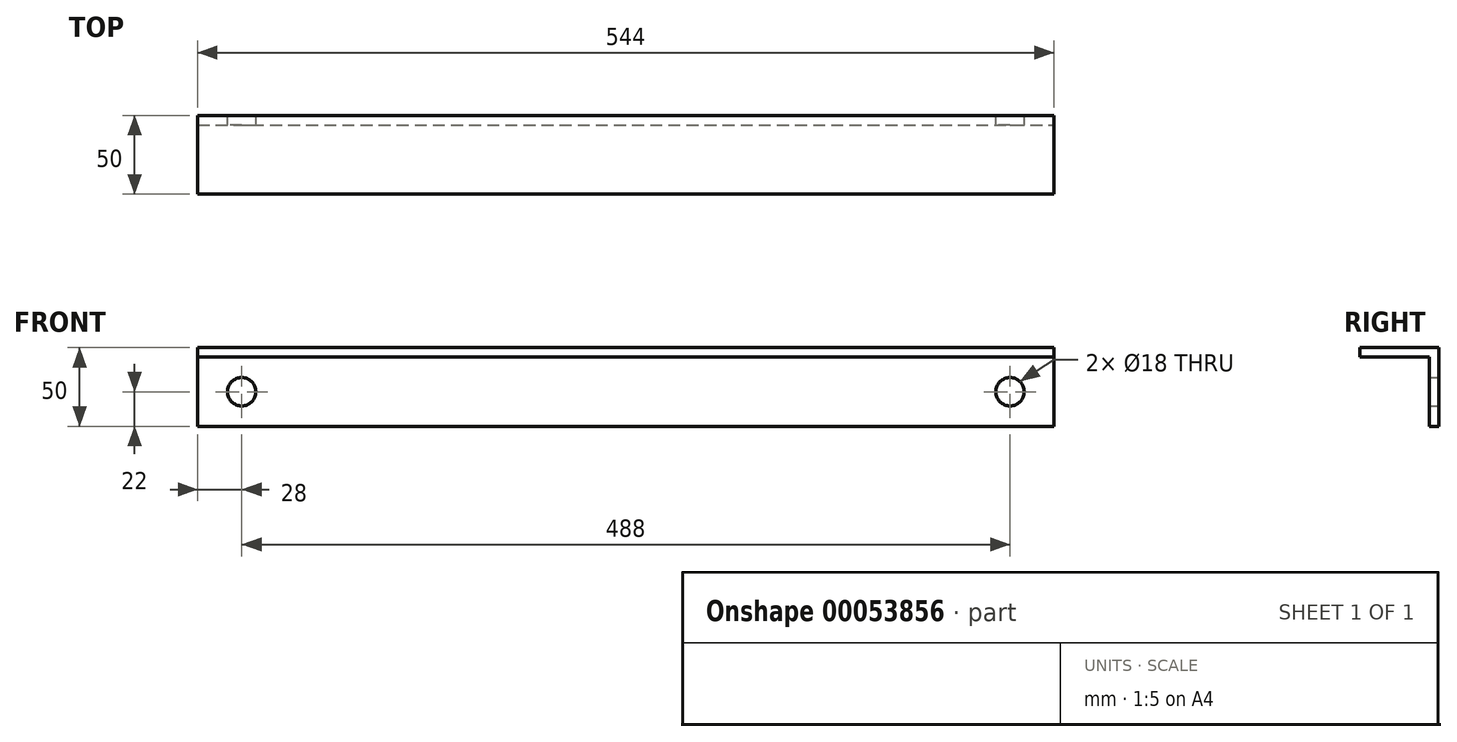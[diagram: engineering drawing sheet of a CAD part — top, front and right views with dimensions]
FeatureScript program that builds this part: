
annotation { "Feature Type Name" : "Feature", "Feature Type Description" : "" }
export const myFeature = defineFeature(function(context is Context, id is Id, definition is map)
    precondition{}
    {
        {
            var Q0;
            Q0=qCreatedBy(makeId("Front.planeOp"),FACE);
            var sketch = newSketch(context, id + "F0", { "sketchPlane" : qUnion([Q0])});
            skLineSegment(sketch, "E0.bottom", {"start": v(0, 0) * mm, "end": v(544, 0) * mm});
            skLineSegment(sketch, "E0.top", {"start": v(0, 50) * mm, "end": v(544, 50) * mm});
            skLineSegment(sketch, "E0.left", {"start": v(0, 0) * mm, "end": v(0, 50) * mm});
            skLineSegment(sketch, "E0.right", {"start": v(544, 0) * mm, "end": v(544, 50) * mm});
            skSolve(sketch);
        }
        {
            var Q0;
            Q0 = qSketchRegion(id + "F0", true);
            extrude(context, id + "F1", {"entities" : qUnion([Q0]), "depth" : 6 * mm});
        }
        {
            var Q0;
            Q0=makeQuery(id+"F1.opExtrude","CAP_FACE",FACE,{"disambiguationData":[OSD([sQuery(id+"F0.wireOp",EDGE,"E0.bottom"),sQuery(id+"F0.wireOp",EDGE,"E0.top"),sQuery(id+"F0.wireOp",EDGE,"E0.left"),sQuery(id+"F0.wireOp",EDGE,"E0.right")])],"isStart":false});
            var sketch = newSketch(context, id + "F2", { "sketchPlane" : qUnion([Q0])});
            skLineSegment(sketch, "E1.bottom", {"start": v(0, 50) * mm, "end": v(544, 50) * mm});
            skLineSegment(sketch, "E1.top", {"start": v(0, 44) * mm, "end": v(544, 44) * mm});
            skLineSegment(sketch, "E1.left", {"start": v(0, 50) * mm, "end": v(0, 44) * mm});
            skLineSegment(sketch, "E1.right", {"start": v(544, 50) * mm, "end": v(544, 44) * mm});
            skSolve(sketch);
        }
        {
            var Q0;
            Q0 = qSketchRegion(id + "F2", true);
            extrude(context, id + "F3", {"entities" : qUnion([Q0]), "operationType" : NewBodyOperationType.ADD, "depth" : 44 * mm});
        }
        {
            var Q0;
            Q0=makeQuery(id+"F1.opExtrude","CAP_FACE",FACE,{"disambiguationData":[OSD([sQuery(id+"F0.wireOp",EDGE,"E0.bottom"),sQuery(id+"F0.wireOp",EDGE,"E0.top"),sQuery(id+"F0.wireOp",EDGE,"E0.left"),sQuery(id+"F0.wireOp",EDGE,"E0.right")])],"isStart":true});
            var sketch = newSketch(context, id + "F4", { "sketchPlane" : qUnion([Q0])});
            skCircle(sketch, "E2", {"center": v(-516, 22) * mm, "radius": 9 * mm});
            skCircle(sketch, "E3", {"center": v(-28, 22) * mm, "radius": 9 * mm});
            skSolve(sketch);
        }
        {
            var Q0;
            Q0 = qSketchRegion(id + "F4", true);
            extrude(context, id + "F5", {"entities" : qUnion([Q0]), "operationType" : NewBodyOperationType.REMOVE, "oppositeDirection" : true, "depth" : 25 * mm});
        }
    });
